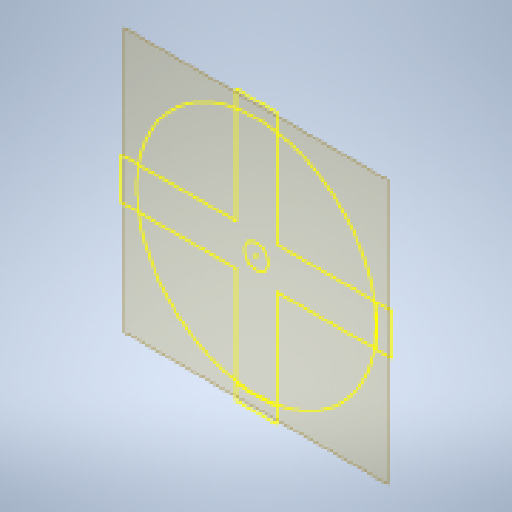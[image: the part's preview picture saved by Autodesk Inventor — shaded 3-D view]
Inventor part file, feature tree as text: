
AUTODESK INVENTOR PART (.ipt)
format: ipt  version: 2023 (Build 270158000, 158)  size: 335,872 bytes
history: native  units: in
note: dims shown in document units (in); Inventor stores cm internally (conversion verified against a paired STEP export)
features: projected_geometry x10, extrude x7, sketch x7, reference x6, other x5
ambient origin geometry x8: Origin, YZ Plane, XZ Plane, XY Plane, X Axis, Y Axis, Z Axis, Center Point
bodies: Body1 (feature_tree)
feature tree (35):
  other  "Bryła1"
  other  "Płaszczyzna konstrukcyjna1"
  extrude  "Wyciągnięcie proste1"  Depth=0.1575in TaperAngle=0.0deg
  extrude  "Wyciągnięcie proste2"  Depth=0.0079in
  extrude  "Wyciągnięcie proste3"  Depth=0.0591in TaperAngle=0.0deg
  extrude  "Wyciągnięcie proste4"  TaperAngle=0.0deg  [1 undecoded]
  extrude  "Wyciągnięcie proste5"  Depth=0.3937in TaperAngle=0.0deg
  extrude  "Wyciągnięcie proste6"  Depth=0.3937in TaperAngle=0.0deg
  extrude  "Wyciągnięcie proste7"  Depth=0.2283in
  sketch  "Szkic1"
  reference  "Odniesienie1"
  reference  "Odniesienie2"
  reference  "Odniesienie3"
  reference  "Odniesienie4"
  sketch  "Szkic2"
  reference  "Odniesienie5"
  reference  "Odniesienie6"
  sketch  "Szkic3"
  projected_geometry  "Pętla rzutowana1"
  projected_geometry  "Pętla rzutowana2"
  projected_geometry  "Pętla rzutowana3"
  projected_geometry  "Pętla rzutowana4"
  sketch  "Szkic4"
  projected_geometry  "Pętla rzutowana5"
  projected_geometry  "Pętla rzutowana6"
  projected_geometry  "Pętla rzutowana7"
  projected_geometry  "Pętla rzutowana8"
  sketch  "Szkic5"
  projected_geometry  "Pętla rzutowana9"
  sketch  "Szkic6"
  sketch  "Szkic7"
  projected_geometry  "Pętla rzutowana10"
  other  "Zespół2"
  other  "podstawa_formy:1"
  other  "gora:1"
note: 1 required parameter value undecoded (feature->parameter linkage not recoverable at this tier; creation-order binding heuristic only, values carry confidence <= 0.55)
